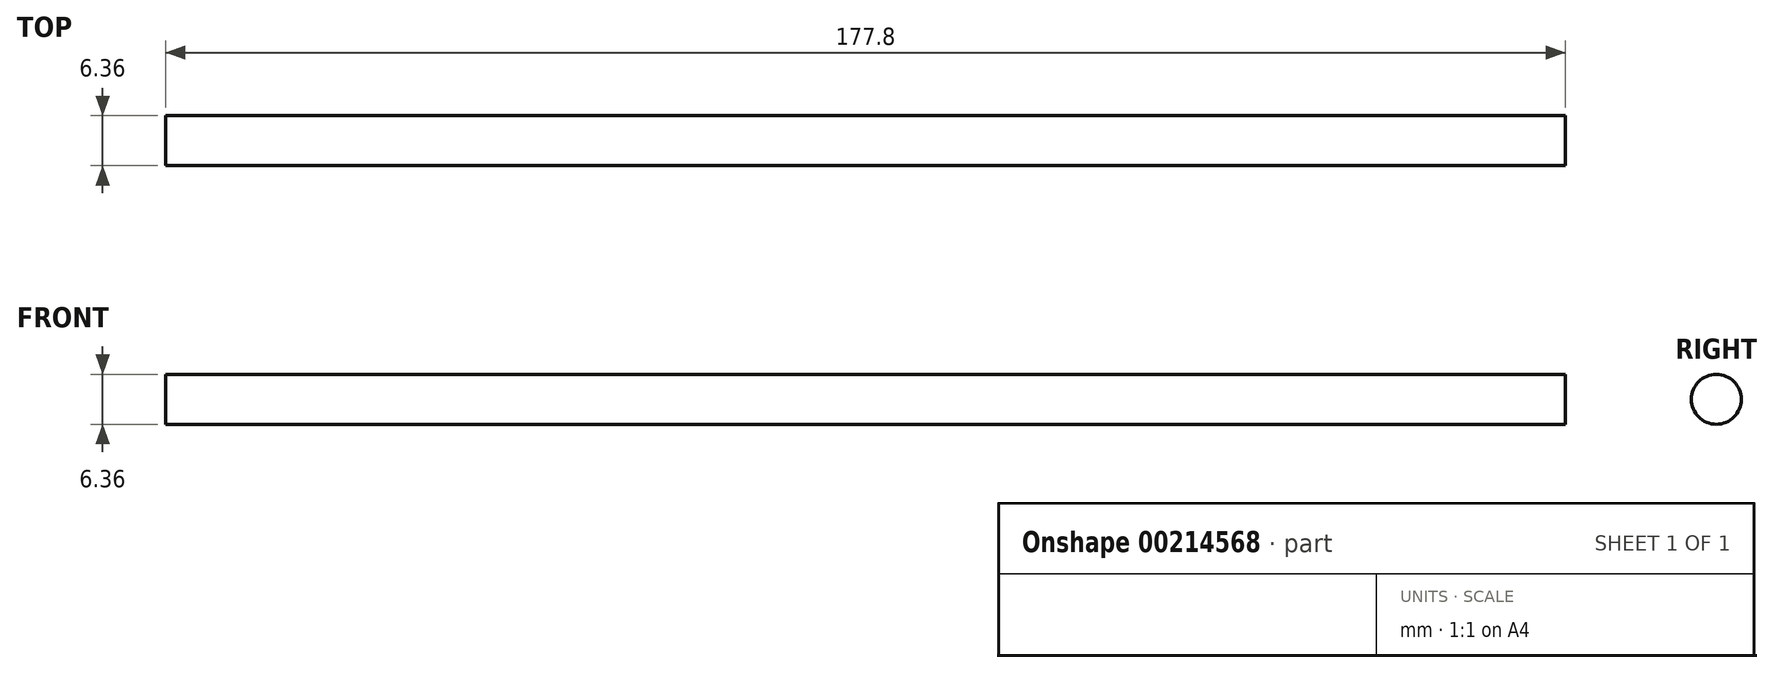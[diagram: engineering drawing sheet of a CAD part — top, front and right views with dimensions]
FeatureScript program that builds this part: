
annotation { "Feature Type Name" : "Feature", "Feature Type Description" : "" }
export const myFeature = defineFeature(function(context is Context, id is Id, definition is map)
    precondition{}
    {
        {
            var Q0;
            Q0=qCreatedBy(makeId("Right.planeOp"),FACE);
            var sketch = newSketch(context, id + "F0", { "sketchPlane" : qUnion([Q0])});
            skCircle(sketch, "E0", {"center": v(0, 0) * mm, "radius": 3.18 * mm});
            skSolve(sketch);
        }
        {
            var Q0;
            Q0=makeQuery(id+"F0.imprint","IMPRINT",FACE,{"disambiguationData":[TD([[makeQuery(id+"F0.imprint","IMPRINT",EDGE,{"derivedFrom":sQuery(id+"F0.wireOp",EDGE,"E0")}),1.0]])]});
            extrude(context, id + "F1", {"entities" : qUnion([Q0]), "depth" : 177.8 * mm, "symmetric" : true});
        }
    });
